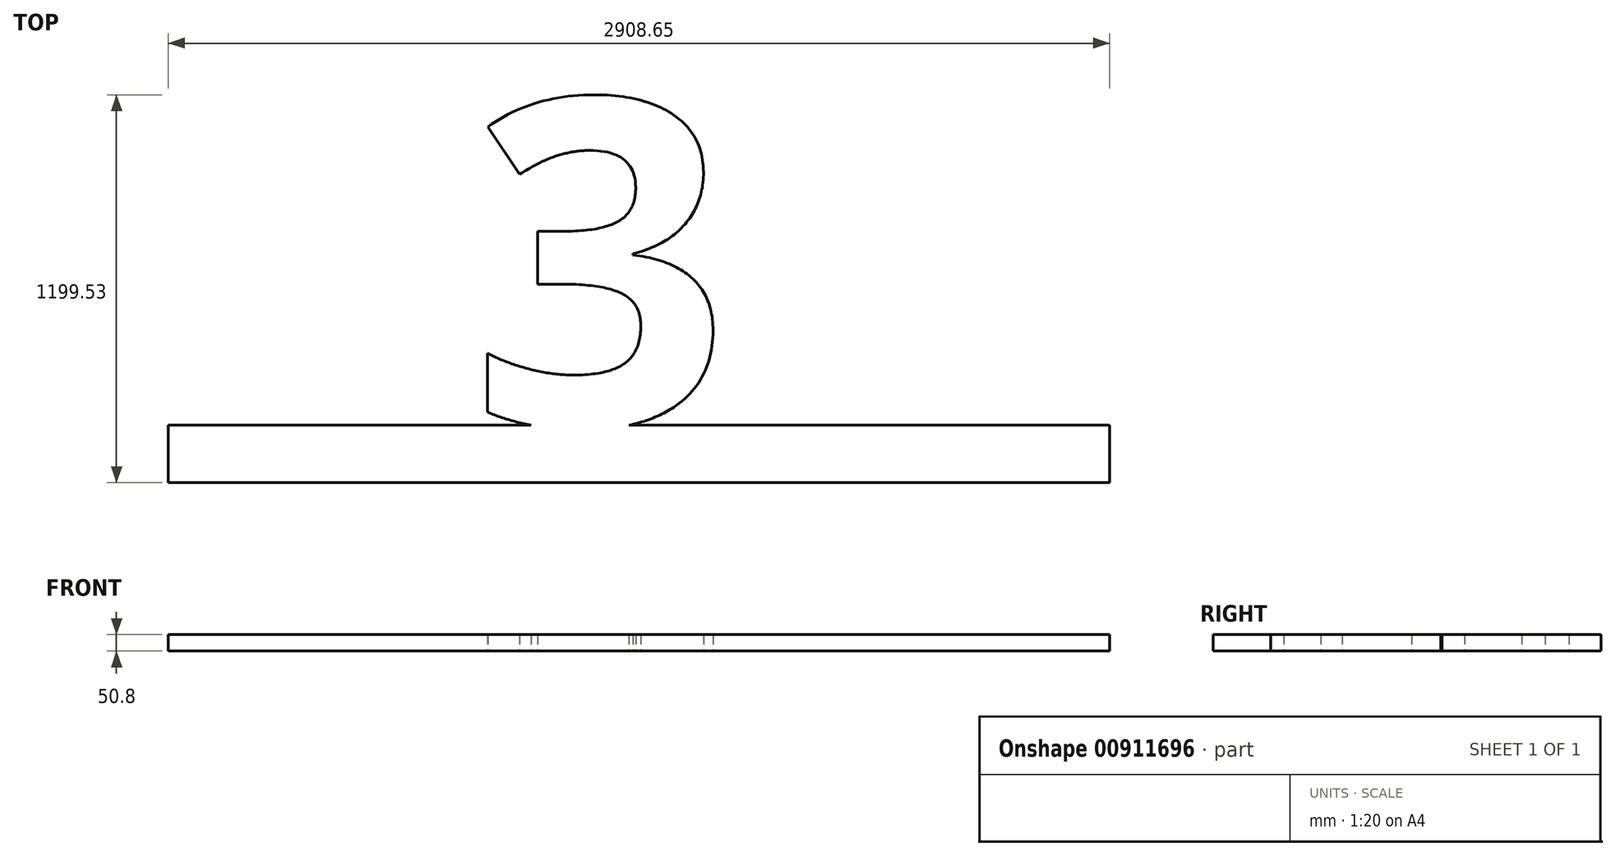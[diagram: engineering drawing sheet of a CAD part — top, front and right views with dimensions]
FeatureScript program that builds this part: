
annotation { "Feature Type Name" : "Feature", "Feature Type Description" : "" }
export const myFeature = defineFeature(function(context is Context, id is Id, definition is map)
    precondition{}
    {
        {
            var Q0;
            Q0=qCreatedBy(makeId("Top.planeOp"),FACE);
            var sketch = newSketch(context, id + "F0", { "sketchPlane" : qUnion([Q0])});
            skLineSegment(sketch, "E0.bottom", {"start": v(-362.77, -177.8) * mm, "end": v(2545.88, -177.8) * mm});
            skLineSegment(sketch, "E0.top", {"start": v(-362.77, 0) * mm, "end": v(2545.88, 0) * mm});
            skLineSegment(sketch, "E0.left", {"start": v(-362.77, -177.8) * mm, "end": v(-362.77, 0) * mm});
            skLineSegment(sketch, "E0.right", {"start": v(2545.88, -177.8) * mm, "end": v(2545.88, 0) * mm});
            skText(sketch, "E1", { "text": "13H", "fontName": "OpenSans-Bold.ttf"});
            const initialGuessF0  = {"E1": [-0.23577, 0, 1, 0, 1.016]};
            skSetInitialGuess(sketch, initialGuessF0);
            skSolve(sketch);
        }
        {
            var Q0;
            {var subQ0=sQuery(id+"F0.wireOp",EDGE,"d5d90416-0cdc-48ac-b64b-d5d0caaf983f.sketch_text.stroke-12");var subQ1=sQuery(id+"F0.wireOp",EDGE,"E0.top");var subQ2=makeQuery(id+"F0.imprint","INTERSECT",VERTEX,{"derivedFrom":[subQ1,subQ0]});Q0=makeQuery(id+"F0.imprint","IMPRINT",FACE,{"disambiguationData":[TD([[makeQuery(id+"F0.imprint","IMPRINT",EDGE,{"disambiguationData":[TD([[subQ2,-1.0]])],"derivedFrom":subQ1}),-1.0]])]});}
            var Q1;
            {var subQ6=sQuery(id+"F0.wireOp",EDGE,"d5d90416-0cdc-48ac-b64b-d5d0caaf983f.sketch_text.stroke-10");Q1=makeQuery(id+"F0.imprint","IMPRINT",FACE,{"disambiguationData":[TD([[makeQuery(id+"F0.imprint","IMPRINT",EDGE,{"derivedFrom":subQ6}),-1.0]])]});}
            var Q2;
            Q2=makeQuery(id+"F0.imprint","IMPRINT",FACE,{"disambiguationData":[TD([[makeQuery(id+"F0.imprint","IMPRINT",EDGE,{"derivedFrom":sQuery(id+"F0.wireOp",EDGE,"E0.bottom")}),1.0]])]});
            var Q3;
            Q3=makeQuery(id+"F0.imprint","IMPRINT",FACE,{"disambiguationData":[TD([[makeQuery(id+"F0.imprint","IMPRINT",EDGE,{"derivedFrom":sQuery(id+"F0.wireOp",EDGE,"d5d90416-0cdc-48ac-b64b-d5d0caaf983f.sketch_text.stroke-26")}),-1.0]])]});
            var Q4;
            Q4=makeQuery(id+"F0.imprint","IMPRINT",FACE,{"disambiguationData":[TD([[makeQuery(id+"F0.imprint","IMPRINT",EDGE,{"derivedFrom":sQuery(id+"F0.wireOp",EDGE,"d5d90416-0cdc-48ac-b64b-d5d0caaf983f.sketch_text.stroke-0")}),-1.0]])]});
            var Q5;
            Q5=makeQuery(id+"F0.imprint","IMPRINT",FACE,{"disambiguationData":[TD([[makeQuery(id+"F0.imprint","IMPRINT",EDGE,{"derivedFrom":sQuery(id+"F0.wireOp",EDGE,"eadfe806-04ac-4918-bb0a-3f37c2bbbc6a.sketch_text.stroke-10")}),-1.0]])]});
            var Q6;
            Q6=makeQuery(id+"F0.imprint","IMPRINT",FACE,{"disambiguationData":[TD([[makeQuery(id+"F0.imprint","IMPRINT",EDGE,{"derivedFrom":sQuery(id+"F0.wireOp",EDGE,"eadfe806-04ac-4918-bb0a-3f37c2bbbc6a.sketch_text.stroke-0")}),-1.0]])]});
            var Q7;
            Q7=makeQuery(id+"F0.imprint","IMPRINT",FACE,{"disambiguationData":[TD([[makeQuery(id+"F0.imprint","IMPRINT",EDGE,{"derivedFrom":sQuery(id+"F0.wireOp",EDGE,"eadfe806-04ac-4918-bb0a-3f37c2bbbc6a.sketch_text.stroke-20")}),-1.0]])]});
            var Q8;
            Q8=makeQuery(id+"F0.imprint","IMPRINT",FACE,{"disambiguationData":[TD([[makeQuery(id+"F0.imprint","IMPRINT",EDGE,{"derivedFrom":sQuery(id+"F0.wireOp",EDGE,"7b9dad4d-f56e-4f66-a96d-e45d99efa82c.sketch_text.stroke-0")}),-1.0]])]});
            var Q9;
            Q9=makeQuery(id+"F0.imprint","IMPRINT",FACE,{"disambiguationData":[TD([[makeQuery(id+"F0.imprint","IMPRINT",EDGE,{"derivedFrom":sQuery(id+"F0.wireOp",EDGE,"7b9dad4d-f56e-4f66-a96d-e45d99efa82c.sketch_text.stroke-10")}),-1.0]])]});
            var Q10;
            Q10=makeQuery(id+"F0.imprint","IMPRINT",FACE,{"disambiguationData":[TD([[makeQuery(id+"F0.imprint","IMPRINT",EDGE,{"derivedFrom":sQuery(id+"F0.wireOp",EDGE,"7b9dad4d-f56e-4f66-a96d-e45d99efa82c.sketch_text.stroke-34")}),-1.0]])]});
            var Q11;
            {var subQ0=sQuery(id+"F0.wireOp",EDGE,"E1.sketch_text.stroke-17");var subQ1=sQuery(id+"F0.wireOp",EDGE,"E0.top");var subQ2=makeQuery(id+"F0.imprint","INTERSECT",VERTEX,{"derivedFrom":[subQ1,subQ0]});Q11=makeQuery(id+"F0.imprint","IMPRINT",FACE,{"disambiguationData":[TD([[makeQuery(id+"F0.imprint","IMPRINT",EDGE,{"disambiguationData":[TD([[subQ2,-1.0]])],"derivedFrom":subQ1}),-1.0]])]});}
            var Q12;
            Q12=makeQuery(id+"F0.imprint","IMPRINT",FACE,{"disambiguationData":[TD([[makeQuery(id+"F0.imprint","IMPRINT",EDGE,{"derivedFrom":sQuery(id+"F0.wireOp",EDGE,"E1.sketch_text.stroke-10")}),-1.0]])]});
            var Q13;
            Q13=makeQuery(id+"F0.imprint","IMPRINT",FACE,{"disambiguationData":[TD([[makeQuery(id+"F0.imprint","IMPRINT",EDGE,{"derivedFrom":sQuery(id+"F0.wireOp",EDGE,"E1.sketch_text.stroke-37")}),-1.0]])]});
            var Q14;
            Q14=makeQuery(id+"F0.imprint","IMPRINT",FACE,{"disambiguationData":[TD([[makeQuery(id+"F0.imprint","IMPRINT",EDGE,{"derivedFrom":sQuery(id+"F0.wireOp",EDGE,"E1.sketch_text.stroke-0")}),-1.0]])]});
            extrude(context, id + "F1", {"entities" : qUnion([Q0, Q1, Q2, Q3, Q4, Q5, Q6, Q7, Q8, Q9, Q10, Q11, Q12, Q13, Q14]), "depth" : 50.8 * mm, "offsetDistance" : 25.4 * mm});
        }
    });
